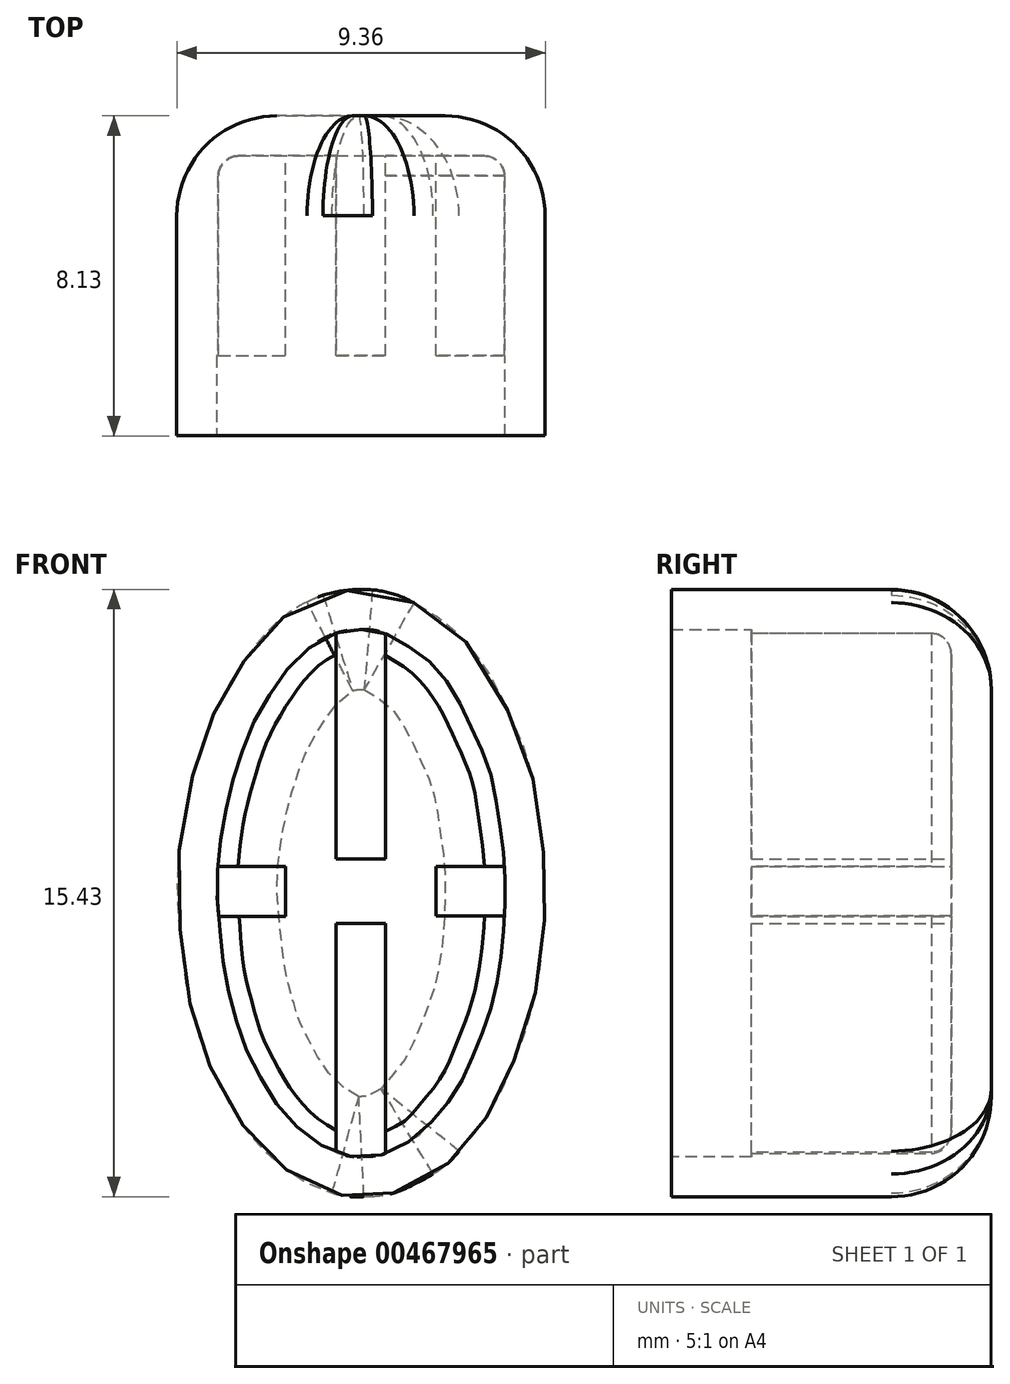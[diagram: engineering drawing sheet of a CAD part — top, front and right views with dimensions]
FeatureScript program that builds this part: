
annotation { "Feature Type Name" : "Feature", "Feature Type Description" : "" }
export const myFeature = defineFeature(function(context is Context, id is Id, definition is map)
    precondition{}
    {
        {
            var Q0;
            Q0=qCreatedBy(makeId("Front.planeOp"),FACE);
            var sketch = newSketch(context, id + "F0", { "sketchPlane" : qUnion([Q0])});
            skFitSpline(sketch, "E0", {"points": [v(-2.97, 5.84) * mm, v(-3.22, 5.46) * mm, v(-3.73, 4.54) * mm, v(-4.04, 3.7) * mm, v(-4.32, 2.77) * mm, v(-4.53, 1.62) * mm, v(-4.67, 0.18) * mm, v(-4.58, -1.08) * mm, v(-4.44, -2.35) * mm, v(-4.2, -3.32) * mm, v(-3.93, -4.2) * mm, v(-3.55, -5) * mm, v(-3.02, -5.9) * mm, v(-2.4, -6.63) * mm, v(-1.87, -7.09) * mm, v(-1.24, -7.48) * mm, v(-0.4, -7.74) * mm, v(0.08, -7.76) * mm, v(0.7, -7.7) * mm, v(1.35, -7.45) * mm, v(2.14, -6.98) * mm, v(2.58, -6.51) * mm, v(3.13, -5.83) * mm, v(3.54, -5.14) * mm, v(3.9, -4.3) * mm, v(4.25, -3.36) * mm, v(4.52, -2.15) * mm, v(4.65, -1) * mm, v(4.68, -0.12) * mm, v(4.65, 0.93) * mm, v(4.5, 2.07) * mm, v(4.28, 3.26) * mm, v(3.86, 4.32) * mm, v(3.3, 5.45) * mm, v(2.47, 6.54) * mm, v(1.75, 7.09) * mm, v(0.97, 7.51) * mm, v(0, 7.67) * mm, v(-1.12, 7.46) * mm, v(-1.95, 6.97) * mm, v(-2.53, 6.42) * mm, v(-2.97, 5.84) * mm]});
            skSolve(sketch);
        }
        {
            var Q0;
            Q0=makeQuery(id+"F0.imprint","IMPRINT",FACE,{"disambiguationData":[TD([[makeQuery(id+"F0.imprint","IMPRINT",EDGE,{"derivedFrom":sQuery(id+"F0.wireOp",EDGE,"E0")}),1.0]])]});
            extrude(context, id + "F1", {"entities" : qUnion([Q0]), "depth" : 8.13 * mm, "offsetDistance" : 25.4 * mm});
        }
        {
            var Q0;
            Q0=makeQuery(id+"F1.opExtrude","CAP_FACE",FACE,{"disambiguationData":[OSD([sQuery(id+"F0.wireOp",EDGE,"E0")])],"isStart":false});
            shell(context, id + "F2", {"entities" : qUnion([Q0]), "thickness" : 1.02 * mm});
        }
        {
            var Q0;
            {var subQ0=sQuery(id+"F0.wireOp",EDGE,"E0");Q0=makeQuery(id+"F2.opShell","OFFSET_FACE",FACE,{"disambiguationData":[OSD([subQ0]),TDD([makeQuery(id+"F1.opExtrude","CAP_FACE",FACE,{"disambiguationData":[OSD([subQ0])],"isStart":true})])]});}
            var sketch = newSketch(context, id + "F3", { "sketchPlane" : qUnion([Q0])});
            skArc(sketch, "E1", {"start": v(-5.06, -1.14) * mm, "mid": v(-3.66, -3.66) * mm, "end": v(-1.14, -5.06) * mm});
            skLineSegment(sketch, "E2", {"start": v(-1.14, -5.06) * mm, "end": v(-1.14, -0.82) * mm});
            skLineSegment(sketch, "E3", {"start": v(1.14, -0.82) * mm, "end": v(-1.14, -0.82) * mm});
            skLineSegment(sketch, "E4", {"start": v(1.14, -0.82) * mm, "end": v(1.14, -5.06) * mm});
            skArc(sketch, "E5", {"start": v(1.14, -5.06) * mm, "mid": v(3.66, -3.66) * mm, "end": v(5.06, -1.14) * mm});
            skLineSegment(sketch, "E6", {"start": v(5.06, -1.14) * mm, "end": v(1.92, -1.14) * mm});
            skLineSegment(sketch, "E7", {"start": v(1.92, 1.14) * mm, "end": v(1.92, -1.14) * mm});
            skLineSegment(sketch, "E8", {"start": v(1.92, 1.14) * mm, "end": v(5.06, 1.14) * mm});
            skArc(sketch, "E9", {"start": v(5.06, 1.14) * mm, "mid": v(3.66, 3.66) * mm, "end": v(1.14, 5.06) * mm});
            skLineSegment(sketch, "E10", {"start": v(1.14, 5.06) * mm, "end": v(1.14, 0.82) * mm});
            skLineSegment(sketch, "E11", {"start": v(-1.14, 0.82) * mm, "end": v(-1.14, 5.06) * mm});
            skArc(sketch, "E12", {"start": v(-1.14, 5.06) * mm, "mid": v(-3.66, 3.66) * mm, "end": v(-5.06, 1.14) * mm});
            skLineSegment(sketch, "E13", {"start": v(-5.06, 1.14) * mm, "end": v(-1.92, 1.14) * mm});
            skLineSegment(sketch, "E14", {"start": v(-1.91, -1.14) * mm, "end": v(-1.91, 1.13) * mm});
            skLineSegment(sketch, "E15", {"start": v(-1.92, -1.15) * mm, "end": v(-5.06, -1.15) * mm});
            skLineSegment(sketch, "E16.0", {"start": v(-0.63, 1.32) * mm, "end": v(-0.63, 5.06) * mm});
            skLineSegment(sketch, "E16.2", {"start": v(0.63, 5.06) * mm, "end": v(0.63, 1.32) * mm});
            skLineSegment(sketch, "E17.0", {"start": v(2.42, 0.63) * mm, "end": v(5.06, 0.63) * mm});
            skLineSegment(sketch, "E17.2", {"start": v(5.06, -0.63) * mm, "end": v(2.42, -0.63) * mm});
            skLineSegment(sketch, "E18.0", {"start": v(0.63, -1.32) * mm, "end": v(0.63, -5.06) * mm});
            skLineSegment(sketch, "E18.2", {"start": v(-0.63, -5.06) * mm, "end": v(-0.63, -1.32) * mm});
            skLineSegment(sketch, "E19.0", {"start": v(-2.42, -0.64) * mm, "end": v(-5.06, -0.64) * mm});
            skLineSegment(sketch, "E19.2", {"start": v(-5.06, 0.63) * mm, "end": v(-2.42, 0.63) * mm});
            skLineSegment(sketch, "E20", {"start": v(-0.63, 1.32) * mm, "end": v(-0.63, 0.82) * mm});
            skLineSegment(sketch, "E21", {"start": v(0.63, 1.32) * mm, "end": v(0.63, 0.82) * mm});
            skLineSegment(sketch, "E22", {"start": v(-2.42, 0.63) * mm, "end": v(-1.91, 0.63) * mm});
            skLineSegment(sketch, "E23", {"start": v(-2.42, -0.64) * mm, "end": v(-1.91, -0.64) * mm});
            skLineSegment(sketch, "E24", {"start": v(-0.63, -1.32) * mm, "end": v(-0.63, -0.82) * mm});
            skLineSegment(sketch, "E25", {"start": v(0.63, -1.32) * mm, "end": v(0.63, -0.82) * mm});
            skLineSegment(sketch, "E26", {"start": v(2.42, 0.63) * mm, "end": v(1.92, 0.63) * mm});
            skLineSegment(sketch, "E27", {"start": v(2.42, -0.63) * mm, "end": v(1.92, -0.63) * mm});
            skPoint(sketch, "E28", {"position": v(-7.57, 0.63) * mm});
            skPoint(sketch, "E29", {"position": v(-7.58, -0.63) * mm});
            skPoint(sketch, "E30", {"position": v(6.62, 0.63) * mm});
            skPoint(sketch, "E31", {"position": v(6.62, -0.63) * mm});
            skLineSegment(sketch, "E32", {"start": v(-5.06, 0.63) * mm, "end": v(-5.06, -0.64) * mm});
            skLineSegment(sketch, "E33", {"start": v(5.06, -0.63) * mm, "end": v(5.06, 0.63) * mm});
            skLineSegment(sketch, "E34", {"start": v(-0.63, -5.06) * mm, "end": v(-0.63, -6.63) * mm});
            skLineSegment(sketch, "E35", {"start": v(0.63, -5.06) * mm, "end": v(0.63, -6.66) * mm});
            skLineSegment(sketch, "E36", {"start": v(-0.63, 5.06) * mm, "end": v(-0.63, 6.56) * mm});
            skLineSegment(sketch, "E37", {"start": v(0.63, 5.06) * mm, "end": v(0.63, 6.55) * mm});
            skLineSegment(sketch, "E38", {"start": v(-0.63, 0.82) * mm, "end": v(0.63, 0.82) * mm});
            skLineSegment(sketch, "E39", {"start": v(-0.63, 6.56) * mm, "end": v(-0.63, 6.95) * mm});
            skLineSegment(sketch, "E40", {"start": v(-0.63, 6.95) * mm, "end": v(0.48, 6.95) * mm});
            skLineSegment(sketch, "E41", {"start": v(0.63, 6.55) * mm, "end": v(0.48, 6.95) * mm});
            skSolve(sketch);
        }
        {
            var Q0;
            {var subQ0=sQuery(id+"F3.wireOp",EDGE,"E22");Q0=makeQuery(id+"F3.imprint","IMPRINT",FACE,{"disambiguationData":[TD([[makeQuery(id+"F3.imprint","IMPRINT",EDGE,{"derivedFrom":subQ0}),-1.0]])]});}
            var Q1;
            {var subQ0=sQuery(id+"F3.wireOp",EDGE,"E26");Q1=makeQuery(id+"F3.imprint","IMPRINT",FACE,{"disambiguationData":[TD([[makeQuery(id+"F3.imprint","IMPRINT",EDGE,{"derivedFrom":subQ0}),1.0]])]});}
            var Q2;
            {var subQ4=sQuery(id+"F3.wireOp",EDGE,"E18.0");Q2=makeQuery(id+"F3.imprint","IMPRINT",FACE,{"disambiguationData":[TD([[makeQuery(id+"F3.imprint","IMPRINT",EDGE,{"derivedFrom":subQ4}),-1.0]])]});}
            var Q3;
            Q3=makeQuery(id+"F3.imprint","IMPRINT",FACE,{"disambiguationData":[TD([[makeQuery(id+"F3.imprint","IMPRINT",EDGE,{"derivedFrom":sQuery(id+"F3.wireOp",EDGE,"E16.0")}),-1.0]])]});
            extrude(context, id + "F4", {"entities" : qUnion([Q0, Q1, Q2, Q3]), "operationType" : NewBodyOperationType.ADD, "depth" : 5.08 * mm, "offsetDistance" : 25.4 * mm});
        }
        {
            var Q0;
            {var subQ0=sQuery(id+"F0.wireOp",EDGE,"E0");Q0=makeQuery(id+"F4.boolean.opBoolean","SPLIT",EDGE,{"disambiguationData":[TD([makeQuery(id+"F4.opExtrude","SWEPT_FACE",FACE,{"disambiguationData":[OSD([sQuery(id+"F3.wireOp",EDGE,"E19.2"),sQuery(id+"F3.wireOp",EDGE,"E22")])]})])],"derivedFrom":makeQuery(id+"F2.opShell","OFFSET_EDGE",EDGE,{"disambiguationData":[OSD([subQ0]),TDD([makeQuery(id+"F1.opExtrude","CAP_EDGE",EDGE,{"disambiguationData":[OSD([subQ0])],"isStart":true})])]})});}
            var Q1;
            {var subQ0=sQuery(id+"F0.wireOp",EDGE,"E0");Q1=makeQuery(id+"F4.boolean.opBoolean","SPLIT",EDGE,{"disambiguationData":[TD([makeQuery(id+"F4.opExtrude","SWEPT_FACE",FACE,{"disambiguationData":[OSD([sQuery(id+"F3.wireOp",EDGE,"E19.0"),sQuery(id+"F3.wireOp",EDGE,"E23")])]})])],"derivedFrom":makeQuery(id+"F2.opShell","OFFSET_EDGE",EDGE,{"disambiguationData":[OSD([subQ0]),TDD([makeQuery(id+"F1.opExtrude","CAP_EDGE",EDGE,{"disambiguationData":[OSD([subQ0])],"isStart":true})])]})});}
            var Q2;
            {var subQ0=sQuery(id+"F0.wireOp",EDGE,"E0");Q2=makeQuery(id+"F4.boolean.opBoolean","SPLIT",EDGE,{"disambiguationData":[TD([makeQuery(id+"F4.opExtrude","SWEPT_FACE",FACE,{"disambiguationData":[OSD([sQuery(id+"F3.wireOp",EDGE,"E17.0"),sQuery(id+"F3.wireOp",EDGE,"E26")])]})])],"derivedFrom":makeQuery(id+"F2.opShell","OFFSET_EDGE",EDGE,{"disambiguationData":[OSD([subQ0]),TDD([makeQuery(id+"F1.opExtrude","CAP_EDGE",EDGE,{"disambiguationData":[OSD([subQ0])],"isStart":true})])]})});}
            var Q3;
            {var subQ0=sQuery(id+"F0.wireOp",EDGE,"E0");Q3=makeQuery(id+"F4.boolean.opBoolean","SPLIT",EDGE,{"disambiguationData":[TD([makeQuery(id+"F4.opExtrude","SWEPT_FACE",FACE,{"disambiguationData":[OSD([sQuery(id+"F3.wireOp",EDGE,"E17.2"),sQuery(id+"F3.wireOp",EDGE,"E27")])]})])],"derivedFrom":makeQuery(id+"F2.opShell","OFFSET_EDGE",EDGE,{"disambiguationData":[OSD([subQ0]),TDD([makeQuery(id+"F1.opExtrude","CAP_EDGE",EDGE,{"disambiguationData":[OSD([subQ0])],"isStart":true})])]})});}
            var Q4;
            Q4=makeQuery(id+"F4.opExtrude","CAP_EDGE",EDGE,{"disambiguationData":[OSD([sQuery(id+"F3.wireOp",EDGE,"E17.2"),sQuery(id+"F3.wireOp",EDGE,"E27")])],"isStart":true});
            var Q5;
            Q5=makeQuery(id+"F4.opExtrude","CAP_EDGE",EDGE,{"disambiguationData":[OSD([sQuery(id+"F3.wireOp",EDGE,"E17.0"),sQuery(id+"F3.wireOp",EDGE,"E26")])],"isStart":true});
            var Q6;
            Q6=makeQuery(id+"F4.opExtrude","CAP_EDGE",EDGE,{"disambiguationData":[OSD([sQuery(id+"F3.wireOp",EDGE,"E16.2"),sQuery(id+"F3.wireOp",EDGE,"E21"),sQuery(id+"F3.wireOp",EDGE,"E37")])],"isStart":true});
            var Q7;
            Q7=makeQuery(id+"F4.opExtrude","CAP_EDGE",EDGE,{"disambiguationData":[OSD([sQuery(id+"F3.wireOp",EDGE,"E16.0"),sQuery(id+"F3.wireOp",EDGE,"E20"),sQuery(id+"F3.wireOp",EDGE,"E36")])],"isStart":true});
            var Q8;
            Q8=makeQuery(id+"F4.opExtrude","CAP_EDGE",EDGE,{"disambiguationData":[OSD([sQuery(id+"F3.wireOp",EDGE,"E19.0"),sQuery(id+"F3.wireOp",EDGE,"E23")])],"isStart":true});
            var Q9;
            Q9=makeQuery(id+"F4.opExtrude","CAP_EDGE",EDGE,{"disambiguationData":[OSD([sQuery(id+"F3.wireOp",EDGE,"E19.2"),sQuery(id+"F3.wireOp",EDGE,"E22")])],"isStart":true});
            var Q10;
            Q10=makeQuery(id+"F4.opExtrude","CAP_EDGE",EDGE,{"disambiguationData":[OSD([sQuery(id+"F3.wireOp",EDGE,"E18.2"),sQuery(id+"F3.wireOp",EDGE,"E24"),sQuery(id+"F3.wireOp",EDGE,"E34")])],"isStart":true});
            var Q11;
            Q11=makeQuery(id+"F4.opExtrude","CAP_EDGE",EDGE,{"disambiguationData":[OSD([sQuery(id+"F3.wireOp",EDGE,"E18.0"),sQuery(id+"F3.wireOp",EDGE,"E25"),sQuery(id+"F3.wireOp",EDGE,"E35")])],"isStart":true});
            var Q12;
            Q12=makeQuery(id+"F4.opExtrude","SWEPT_EDGE",EDGE,{"disambiguationData":[OSD([sQuery(id+"F0.wireOp",EDGE,"E0"),sQuery(id+"F3.wireOp",EDGE,"E19.0")])]});
            var Q13;
            Q13=makeQuery(id+"F4.opExtrude","SWEPT_EDGE",EDGE,{"disambiguationData":[OSD([sQuery(id+"F0.wireOp",EDGE,"E0"),sQuery(id+"F3.wireOp",EDGE,"E19.2")])]});
            var Q14;
            Q14=makeQuery(id+"F4.opExtrude","SWEPT_EDGE",EDGE,{"disambiguationData":[OSD([sQuery(id+"F0.wireOp",EDGE,"E0"),sQuery(id+"F3.wireOp",EDGE,"E36"),sQuery(id+"F3.wireOp",EDGE,"E39")])]});
            var Q15;
            Q15=makeQuery(id+"F4.opExtrude","SWEPT_EDGE",EDGE,{"disambiguationData":[OSD([sQuery(id+"F0.wireOp",EDGE,"E0"),sQuery(id+"F3.wireOp",EDGE,"E37"),sQuery(id+"F3.wireOp",EDGE,"E41")])]});
            var Q16;
            Q16=makeQuery(id+"F4.opExtrude","SWEPT_EDGE",EDGE,{"disambiguationData":[OSD([sQuery(id+"F0.wireOp",EDGE,"E0"),sQuery(id+"F3.wireOp",EDGE,"E17.2")])]});
            var Q17;
            Q17=makeQuery(id+"F4.opExtrude","SWEPT_EDGE",EDGE,{"disambiguationData":[OSD([sQuery(id+"F0.wireOp",EDGE,"E0"),sQuery(id+"F3.wireOp",EDGE,"E17.0")])]});
            var Q18;
            Q18=makeQuery(id+"F4.opExtrude","SWEPT_EDGE",EDGE,{"disambiguationData":[OSD([sQuery(id+"F0.wireOp",EDGE,"E0"),sQuery(id+"F3.wireOp",EDGE,"E34")])]});
            var Q19;
            Q19=makeQuery(id+"F4.opExtrude","SWEPT_EDGE",EDGE,{"disambiguationData":[OSD([sQuery(id+"F0.wireOp",EDGE,"E0"),sQuery(id+"F3.wireOp",EDGE,"E35")])]});
            fillet(context, id + "F5", {"entities" : qUnion([Q0, Q1, Q2, Q3, Q4, Q5, Q6, Q7, Q8, Q9, Q10, Q11, Q12, Q13, Q14, Q15, Q16, Q17, Q18, Q19]), "radius" : 0.5 * mm, "tangentPropagation" : true, "allowEdgeOverflow" : false});
        }
        {
            var Q0;
            Q0=makeQuery(id+"F1.opExtrude","CAP_EDGE",EDGE,{"disambiguationData":[OSD([sQuery(id+"F0.wireOp",EDGE,"E0")])],"isStart":true});
            fillet(context, id + "F6", {"entities" : qUnion([Q0]), "radius" : 2.54 * mm, "tangentPropagation" : true, "allowEdgeOverflow" : false});
        }
    });
